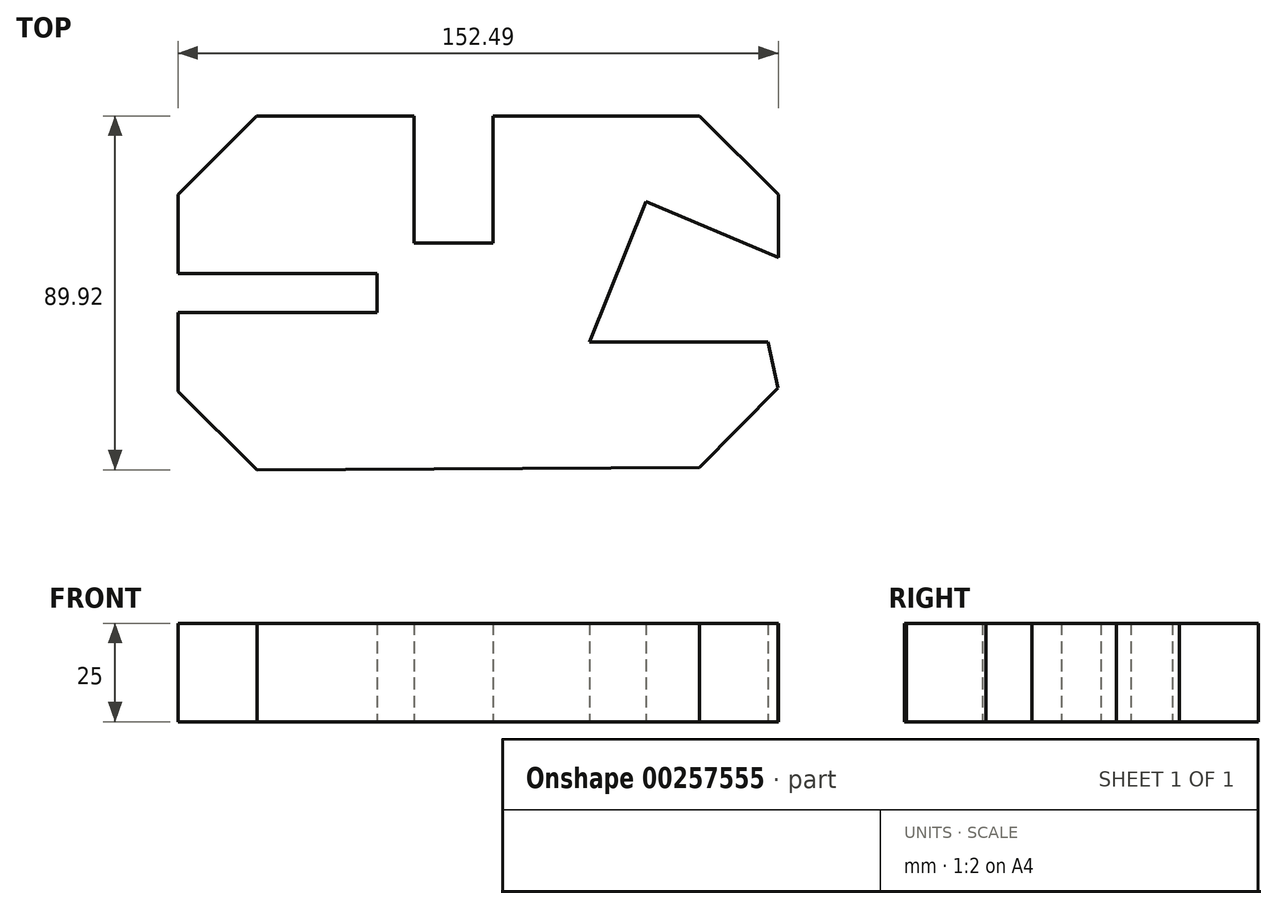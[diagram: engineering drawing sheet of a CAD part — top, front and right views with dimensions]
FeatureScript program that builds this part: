
annotation { "Feature Type Name" : "Feature", "Feature Type Description" : "" }
export const myFeature = defineFeature(function(context is Context, id is Id, definition is map)
    precondition{}
    {
        {
            var Q0;
            Q0=qCreatedBy(makeId("Top.planeOp"),FACE);
            var sketch = newSketch(context, id + "F0", { "sketchPlane" : qUnion([Q0])});
            skLineSegment(sketch, "E0", {"start": v(-77.45, -75.44) * mm, "end": v(34.95, -74.83) * mm});
            skLineSegment(sketch, "E1", {"start": v(34.95, -74.83) * mm, "end": v(54.85, -54.7) * mm});
            skLineSegment(sketch, "E2", {"start": v(54.85, -54.7) * mm, "end": v(52.25, -43) * mm});
            skLineSegment(sketch, "E3", {"start": v(52.25, -43) * mm, "end": v(6.95, -43) * mm});
            skLineSegment(sketch, "E4", {"start": v(6.95, -43) * mm, "end": v(21.38, -7.3) * mm});
            skLineSegment(sketch, "E5", {"start": v(21.38, -7.3) * mm, "end": v(54.92, -21.53) * mm});
            skLineSegment(sketch, "E6", {"start": v(54.92, -21.53) * mm, "end": v(54.92, -5.53) * mm});
            skLineSegment(sketch, "E7", {"start": v(54.92, -5.53) * mm, "end": v(34.91, 14.48) * mm});
            skLineSegment(sketch, "E8", {"start": v(34.91, 14.48) * mm, "end": v(-17.49, 14.48) * mm});
            skLineSegment(sketch, "E9", {"start": v(-17.49, 14.48) * mm, "end": v(-17.56, -17.82) * mm});
            skLineSegment(sketch, "E10", {"start": v(-17.56, -17.82) * mm, "end": v(-37.56, -17.82) * mm});
            skLineSegment(sketch, "E11", {"start": v(-37.56, -17.82) * mm, "end": v(-37.56, 14.48) * mm});
            skLineSegment(sketch, "E12", {"start": v(-37.56, 14.48) * mm, "end": v(-77.56, 14.48) * mm});
            skLineSegment(sketch, "E13", {"start": v(-77.56, 14.48) * mm, "end": v(-97.57, -5.53) * mm});
            skLineSegment(sketch, "E14", {"start": v(-97.57, -5.53) * mm, "end": v(-97.57, -25.53) * mm});
            skLineSegment(sketch, "E15", {"start": v(-97.57, -25.53) * mm, "end": v(-47.07, -25.53) * mm});
            skLineSegment(sketch, "E16", {"start": v(-47.07, -25.53) * mm, "end": v(-47.07, -35.53) * mm});
            skLineSegment(sketch, "E17", {"start": v(-47.07, -35.53) * mm, "end": v(-97.57, -35.53) * mm});
            skLineSegment(sketch, "E18", {"start": v(-97.57, -35.53) * mm, "end": v(-97.57, -55.53) * mm});
            skLineSegment(sketch, "E19", {"start": v(-97.57, -55.53) * mm, "end": v(-77.45, -75.44) * mm});
            skSolve(sketch);
        }
        {
            var Q0;
            Q0=makeQuery(id+"F0.imprint","IMPRINT",FACE,{"disambiguationData":[TD([[makeQuery(id+"F0.imprint","IMPRINT",EDGE,{"derivedFrom":sQuery(id+"F0.wireOp",EDGE,"E0")}),1.0]])]});
            extrude(context, id + "F1", {"entities" : qUnion([Q0]), "depth" : 25 * mm});
        }
    });
